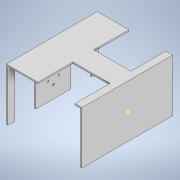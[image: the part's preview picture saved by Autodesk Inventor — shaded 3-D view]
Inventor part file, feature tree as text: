
AUTODESK INVENTOR PART (.ipt)
format: ipt  version: 2020 (Build 240168000, 168)  size: 318,976 bytes
history: native  units: in
note: dims shown in document units (in); Inventor stores cm internally (conversion verified against a paired STEP export)
features: sketch x18, extrude x16
ambient origin geometry x8: Origin, YZ Plane, XZ Plane, XY Plane, X Axis, Y Axis, Z Axis, Center Point
bodies: Solid1 (feature_tree)
feature tree (34):
  extrude  "Extrusion1"  Depth=3.75in
  extrude  "Extrusion3"  Depth=1.5in
  sketch  "Sketch4"  dims[d13=2.5in d14=510.35in d15=0.0in]
  extrude  "Extrusion4"  Depth=2.5in TaperAngle=0.0deg
  sketch  "Sketch6"  dims[d18=8.0in d19=0.0in d20=1.0in d21=0.0in]
  extrude  "Extrusion5"  Depth=0.1in
  extrude  "Extrusion6"  Depth=1.0in TaperAngle=0.0deg
  extrude  "Extrusion7"  Depth=2.0in
  extrude  "Extrusion8"  Depth=1.5in
  extrude  "Extrusion9"  Depth=1.5in
  extrude  "Extrusion10"  Depth=0.25in
  extrude  "Extrusion11"  Depth=0.1in TaperAngle=0.0deg
  extrude  "Extrusion12"  Depth=0.1in TaperAngle=0.0deg
  extrude  "Extrusion13"  Depth=0.5in
  extrude  "Extrusion14"  Depth=0.1in TaperAngle=0.0deg
  extrude  "Extrusion15"  Depth=0.5in
  extrude  "Extrusion16"  Depth=0.1in TaperAngle=0.0deg
  extrude  "Extrusion17"  Depth=0.1406in
  sketch  "Sketch1"  dims[d0=6.5in d1=3.75in]
  sketch  "Sketch3"  dims[d2=5.45in d3=0.0in d12=1.5in]
  sketch  "Sketch5"  dims[d16=0.1in d17=0.1in]
  sketch  "Sketch7"  dims[d22=0.25in d23=2.0in]
  sketch  "Sketch8"  dims[d24=0.25in d25=1.5in]
  sketch  "Sketch9"  dims[d26=0.5in d27=1.5in]
  sketch  "Sketch10"  dims[d28=1.0in d29=0.0in d30=0.25in]
  sketch  "Sketch11"  dims[d31=0.25in d32=0.1in d33=0.0in]
  sketch  "Sketch12"  dims[d34=3.5in d35=0.1in d36=0.0in]
  sketch  "Sketch13"  dims[d37=0.5in d38=0.5in]
  sketch  "Sketch14"  dims[d39=0.5in d40=0.1in d41=0.0in]
  sketch  "Sketch15"  dims[d42=0.5in d43=0.5in]
  sketch  "Sketch16"  dims[d44=0.1in d45=0.0in d46=0.1in d47=0.0in]
  sketch  "Sketch17"  dims[d49=0.1406in d50=0.1406in]
  sketch  "Sketch18"  dims[d51=0.1406in]
  sketch  "Sketch19"  dims[d52=0.1406in d53=0.1in d54=0.0in d55=6.0in d56=0.0in d57=1.75in d58=0.1in d59=0.0in d60=0.05in d61=0.1in d62=6.5in d63=0.0in d64=0.05in d65=6.5in d66=0.0in d67=0.05in d68=0.0in d71=0.1406in d72=0.1406in d73=0.1406in d74=0.1406in]
